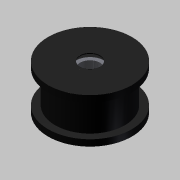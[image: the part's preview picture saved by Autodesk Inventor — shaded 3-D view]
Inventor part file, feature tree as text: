
AUTODESK INVENTOR PART (.ipt)
format: ipt  version: 2012 SP1 (Build 160190100, 190)  size: 153,088 bytes
history: native  units: in
note: dims shown in document units (in); Inventor stores cm internally (conversion verified against a paired STEP export)
features: other x7, extrude x2, sketch x2
ambient origin geometry x8: Origin, YZ Plane, XZ Plane, XY Plane, X Axis, Y Axis, Z Axis, Center Point
bodies: Solid1 (feature_tree)
feature tree (11):
  other  "MSK01-06A"
  other  "BEARING_5_16_5.ipt:1"
  other  "BEARING_5_16_5.ipt:2"
  other  "B17023.ipt:1"
  other  "MSK01-06A_Bodies"
  extrude  "Extrusion1"  Depth=0.25in
  extrude  "Extrusion2"  Depth=0.0001in TaperAngle=0.0deg
  other  "Srf1"
  other  "B30041.ipt:1"
  sketch  "Sketch1"  dims[d0=0.3937in d1=0.25in]
  sketch  "Sketch2"  dims[d2=0.0001in d3=0.0in d4=0.0001in d5=0.0in]
